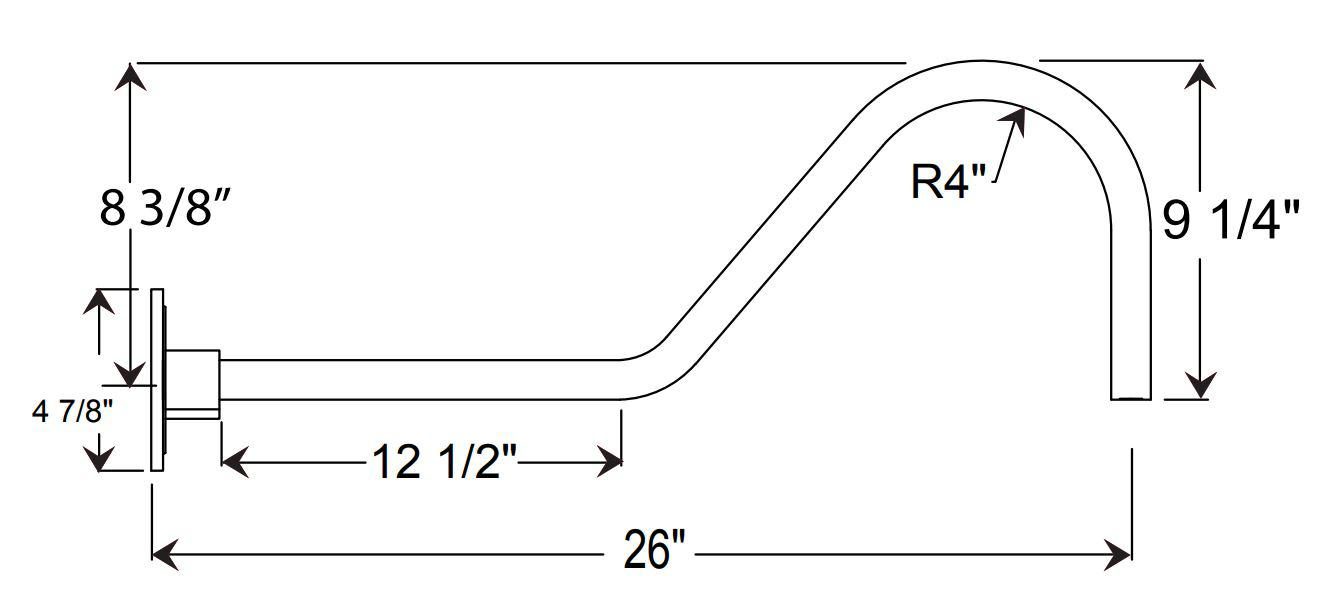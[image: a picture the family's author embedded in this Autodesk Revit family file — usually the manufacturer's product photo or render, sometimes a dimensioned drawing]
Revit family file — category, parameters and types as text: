
# Revit family: OSNC LED 24,36,40
name_source: partatom
category: Lighting Fixtures
units: mm (PartAtom-declared; Revit-internal decimal feet)

## family parameters
Always vertical = Yes
Cut with Voids When Loaded = No
Light Source = Yes
OmniClass Number = 23.80.70.00
OmniClass Title = Lighting
Part Type = Normal
Room Calculation Point = No
Round Connector Dimension = Use Diameter
Shared = No
Work Plane-Based = No

## types (3) — shared parameters
Apparent Load = 37 VA
Body Colour = Spun aluminium
Body Material = body
Bulb = Glass
CRI = >90
Canopy Body = BLACK
Color Filter = 16777215
Construction Material = Heavy Duty spun aluminum.
Default Elevation = 0' - 0"
Description = 120-277 Voltage
Dimming = 1%
Dimming Lamp Color Temperature Shift = <None>
Efficiency = 65-125 lumens per watt
INSIDE BODY = white
Lamp = LED
Life = L70 50,000 hours
Load Classification = Lighting
Manufacturer = ANP Lighting
Photometric Web File = generic
Power Factor = 1
Tilt Angle = 90.00°
URL = https://www.anplighting.com
Voltage = 120 V
Warranty = 5 year limited warranty
Wattage Comments = 37 W

## per-type parameters (varying)
| type | Fixture Diameter | Fixture Height | OSNC24 | OSNC36 | OSNC40 | Weight | a | b |
| OSNC24 | 2' - 0" | 1' - 6" | Yes | No | No | 14.5 lbs | 1' - 6" | 0' - 2" |
| OSNC36 | 3' - 0" | 2' - 3" | No | Yes | No | 25.0 lbs | 2' - 3" | 0' - 4" |
| OSNC40 | 3' - 4" | 2' - 6" | No | No | Yes | 29.0 lbs | 2' - 6" | 0' - 5" |

note: column(s) folded — value = type name in every type: Model

## geometry (parser evidence)
native form markers: Sweep x34
no freeform markers — native parametric forms only
